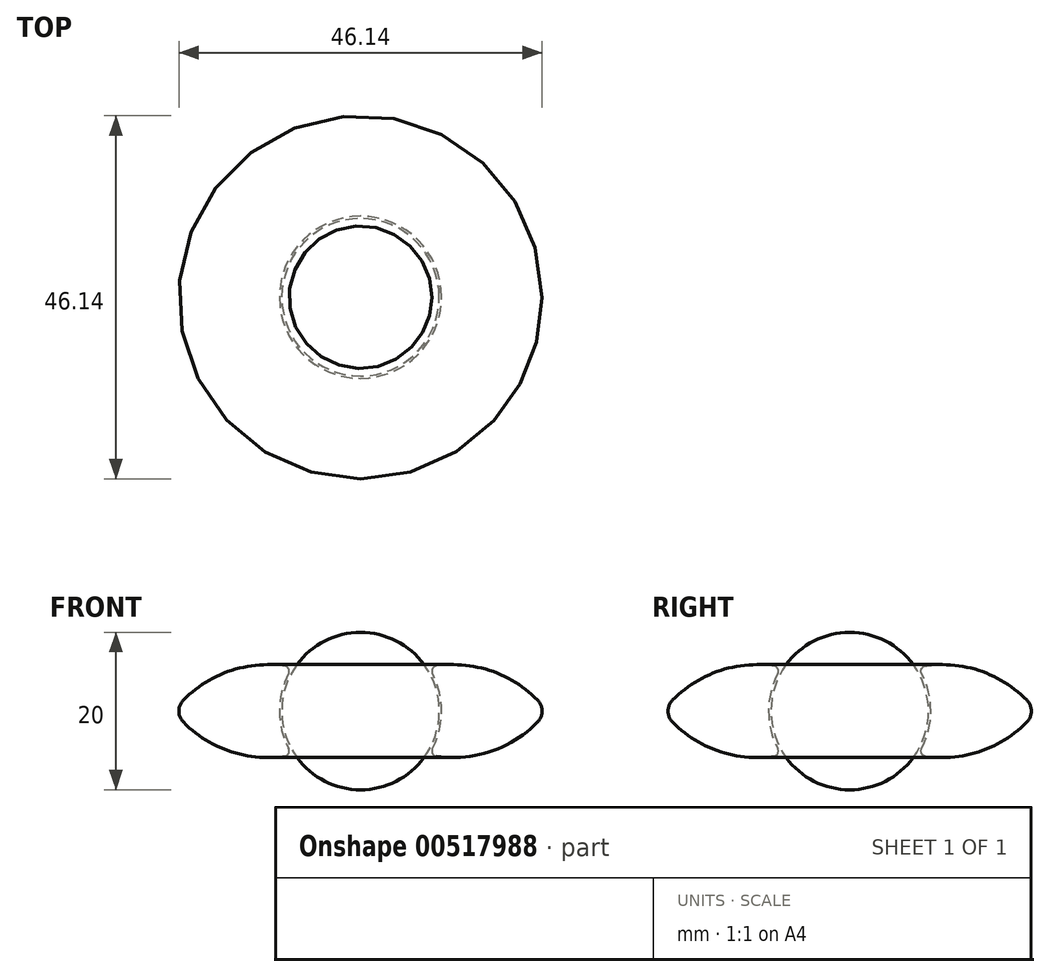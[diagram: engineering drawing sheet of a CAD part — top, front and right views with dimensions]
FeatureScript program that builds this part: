
annotation { "Feature Type Name" : "Feature", "Feature Type Description" : "" }
export const myFeature = defineFeature(function(context is Context, id is Id, definition is map)
    precondition{}
    {
        {
            var Q0;
            Q0=qCreatedBy(makeId("Front.planeOp"),FACE);
            var sketch = newSketch(context, id + "F0", { "sketchPlane" : qUnion([Q0])});
            skLineSegment(sketch, "E0", {"start": v(0, 18.26) * mm, "end": v(0, -14.97) * mm, "construction": true});
            skLineSegment(sketch, "E1", {"start": v(-15.35, 0) * mm, "end": v(19.9, 0) * mm, "construction": true});
            skArc(sketch, "E2", {"start": v(0, -10) * mm, "mid": v(10, 0) * mm, "end": v(0, 10) * mm});
            skLineSegment(sketch, "E3", {"start": v(0, 10) * mm, "end": v(0, -10) * mm});
            skSolve(sketch);
        }
        {
            var Q0;
            Q0=qCreatedBy(makeId("Front.planeOp"),FACE);
            var sketch = newSketch(context, id + "F1", { "sketchPlane" : qUnion([Q0])});
            skArc(sketch, "E4.0", {"start": v(10.3, 0) * mm, "mid": v(10, 2.45) * mm, "end": v(9.14, 4.76) * mm});
            skArc(sketch, "E5", {"start": v(9.64, 5.74) * mm, "mid": v(9.13, 5.38) * mm, "end": v(9.14, 4.76) * mm});
            skArc(sketch, "E6", {"start": v(22.5, 1.4) * mm, "mid": v(16.6, 5.1) * mm, "end": v(9.64, 5.74) * mm});
            skPoint(sketch, "E7.start.orphan", {"position": v(10.3, 0) * mm});
            skLineSegment(sketch, "E8", {"start": v(19.9, 0) * mm, "end": v(22.73, 0) * mm, "construction": true});
            skArc(sketch, "E9.MirrorCS", {"start": v(10.3, 0) * mm, "mid": v(10, -2.45) * mm, "end": v(9.14, -4.76) * mm});
            skArc(sketch, "E10.MirrorCS", {"start": v(9.64, -5.74) * mm, "mid": v(9.13, -5.38) * mm, "end": v(9.14, -4.76) * mm});
            skArc(sketch, "E11.MirrorCS", {"start": v(22.5, -1.4) * mm, "mid": v(16.6, -5.1) * mm, "end": v(9.64, -5.74) * mm});
            skArc(sketch, "E12", {"start": v(22.5, -1.4) * mm, "mid": v(23.07, 0) * mm, "end": v(22.5, 1.4) * mm});
            skLineSegment(sketch, "E13", {"start": v(0, 0) * mm, "end": v(9.14, 4.76) * mm, "construction": true});
            skLineSegment(sketch, "E14", {"start": v(0, 0) * mm, "end": v(9.14, -4.76) * mm, "construction": true});
            skLineSegment(sketch, "E15", {"start": v(10, 0) * mm, "end": v(10, -12.16) * mm, "construction": true});
            skLineSegment(sketch, "E16", {"start": v(9.06, -12.71) * mm, "end": v(9.06, 7.03) * mm, "construction": true});
            skSolve(sketch);
        }
        {
            var Q0;
            Q0=makeQuery(id+"F0.imprint","IMPRINT",FACE,{"disambiguationData":[TD([[makeQuery(id+"F0.imprint","IMPRINT",EDGE,{"derivedFrom":sQuery(id+"F0.wireOp",EDGE,"E2")}),1.0]])]});
            var Q1;
            Q1=makeQuery(id+"F1.imprint","IMPRINT",FACE,{"disambiguationData":[TD([[makeQuery(id+"F1.imprint","IMPRINT",EDGE,{"derivedFrom":sQuery(id+"F1.wireOp",EDGE,"E4.0")}),-1.0]])]});
            var Q2;
            Q2=sQuery(id+"F0.wireOp",EDGE,"E0");
            revolve(context, id + "F2", {"entities" : qUnion([Q0, Q1]), "axis" : qUnion([Q2]), "revolveType" : RevolveType.FULL});
        }
    });
